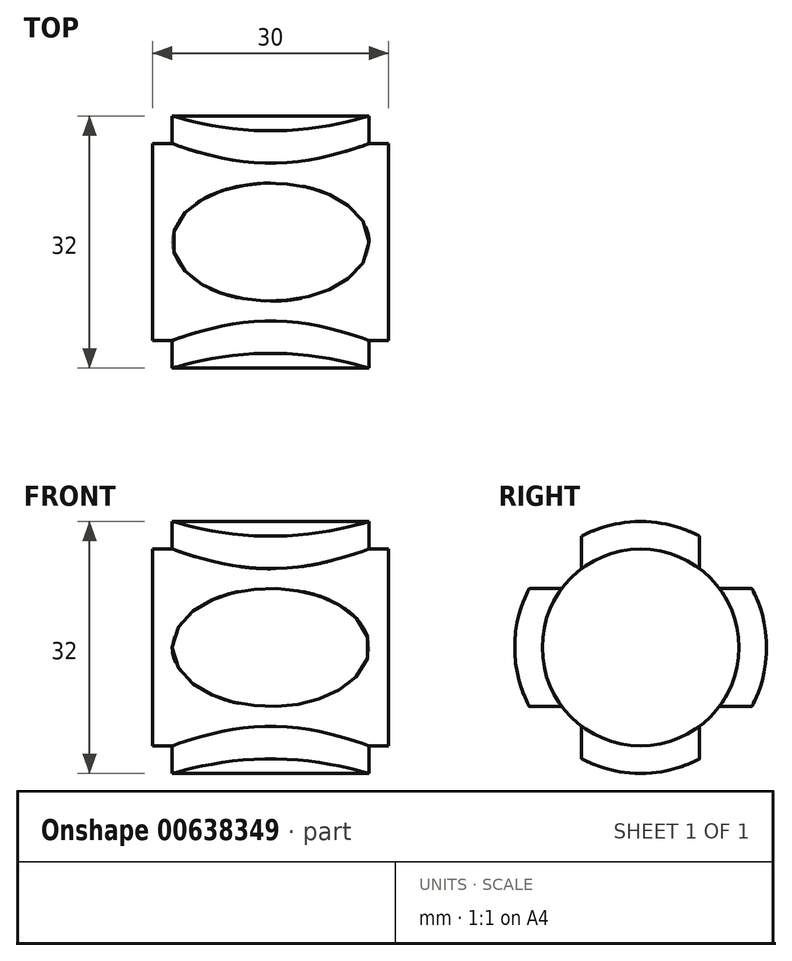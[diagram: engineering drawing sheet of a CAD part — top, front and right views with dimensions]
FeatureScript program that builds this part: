
annotation { "Feature Type Name" : "Feature", "Feature Type Description" : "" }
export const myFeature = defineFeature(function(context is Context, id is Id, definition is map)
    precondition{}
    {
        {
            var Q0;
            Q0=qCreatedBy(makeId("Right.planeOp"),FACE);
            var sketch = newSketch(context, id + "F0", { "sketchPlane" : qUnion([Q0])});
            skLineSegment(sketch, "E0.bottom", {"start": v(-5, 5) * mm, "end": v(5, 5) * mm});
            skLineSegment(sketch, "E0.top", {"start": v(-5, -5) * mm, "end": v(5, -5) * mm});
            skLineSegment(sketch, "E0.left", {"start": v(-5, 5) * mm, "end": v(-5, -5) * mm});
            skLineSegment(sketch, "E0.right", {"start": v(5, 5) * mm, "end": v(5, -5) * mm});
            skSolve(sketch);
        }
        {
            var Q0;
            Q0=makeQuery(id+"F0.imprint","IMPRINT",FACE,{"disambiguationData":[TD([[makeQuery(id+"F0.imprint","IMPRINT",EDGE,{"derivedFrom":sQuery(id+"F0.wireOp",EDGE,"E0.bottom")}),-1.0]])]});
            extrude(context, id + "F1", {"entities" : qUnion([Q0]), "endBound" : BoundingType.SYMMETRIC, "depth" : 30 * mm, "offsetDistance" : 25 * mm});
        }
        {
            var Q0;
            Q0=makeQuery(id+"F1.opExtrude","SWEPT_FACE",FACE,{"disambiguationData":[OSD([sQuery(id+"F0.wireOp",EDGE,"E0.bottom")])]});
            var sketch = newSketch(context, id + "F2", { "sketchPlane" : qUnion([Q0])});
            skText(sketch, "E1", { "text": "3D", "fontName": "OpenSans-Bold.ttf"});
            const initialGuessF2  = {"E1": [-0.00737, -0.00415, 1, 0, 0.00816]};
            skSetInitialGuess(sketch, initialGuessF2);
            skSolve(sketch);
        }
        {
            var Q0;
            Q0=makeQuery(id+"F1.opExtrude","SWEPT_FACE",FACE,{"disambiguationData":[OSD([sQuery(id+"F0.wireOp",EDGE,"E0.left")])]});
            var sketch = newSketch(context, id + "F3", { "sketchPlane" : qUnion([Q0])});
            skText(sketch, "E2", { "text": "3D", "fontName": "OpenSans-Bold.ttf"});
            const initialGuessF3  = {"E2": [-0.00747, -0.004, 1, 0, 0.00816]};
            skSetInitialGuess(sketch, initialGuessF3);
            skSolve(sketch);
        }
        {
            var Q0;
            Q0=makeQuery(id+"F1.opExtrude","SWEPT_FACE",FACE,{"disambiguationData":[OSD([sQuery(id+"F0.wireOp",EDGE,"E0.top")])]});
            var sketch = newSketch(context, id + "F4", { "sketchPlane" : qUnion([Q0])});
            skText(sketch, "E3", { "text": "3D", "fontName": "OpenSans-Bold.ttf"});
            const initialGuessF4  = {"E3": [-0.00747, -0.00412, 1, 0, 0.00816]};
            skSetInitialGuess(sketch, initialGuessF4);
            skSolve(sketch);
        }
        {
            var Q0;
            Q0=makeQuery(id+"F1.opExtrude","SWEPT_FACE",FACE,{"disambiguationData":[OSD([sQuery(id+"F0.wireOp",EDGE,"E0.right")])]});
            var sketch = newSketch(context, id + "F5", { "sketchPlane" : qUnion([Q0])});
            skText(sketch, "E4", { "text": "3D", "fontName": "OpenSans-Bold.ttf"});
            const initialGuessF5  = {"E4": [-0.0075, -0.0041, 1, 0, 0.00816]};
            skSetInitialGuess(sketch, initialGuessF5);
            skSolve(sketch);
        }
        {
            var Q0;
            Q0 = qSketchRegion(id + "F5", true);
            extrude(context, id + "F6", {"entities" : qUnion([Q0]), "operationType" : NewBodyOperationType.ADD, "depth" : 25 * mm, "offsetDistance" : 25 * mm});
        }
        {
            var Q0;
            Q0 = qSketchRegion(id + "F3", true);
            extrude(context, id + "F7", {"entities" : qUnion([Q0]), "operationType" : NewBodyOperationType.ADD, "depth" : 25 * mm, "offsetDistance" : 25 * mm});
        }
        {
            var Q0;
            Q0 = qSketchRegion(id + "F2", true);
            extrude(context, id + "F8", {"entities" : qUnion([Q0]), "operationType" : NewBodyOperationType.ADD, "depth" : 25 * mm, "offsetDistance" : 25 * mm});
        }
        {
            var Q0;
            Q0 = qSketchRegion(id + "F4", true);
            extrude(context, id + "F9", {"entities" : qUnion([Q0]), "operationType" : NewBodyOperationType.ADD, "depth" : 25 * mm, "offsetDistance" : 25 * mm});
        }
        {
            var Q0;
            Q0=qCreatedBy(makeId("Right.planeOp"),FACE);
            var sketch = newSketch(context, id + "F10", { "sketchPlane" : qUnion([Q0])});
            skCircle(sketch, "E5", {"center": v(0, 0) * mm, "radius": 12.5 * mm});
            skSolve(sketch);
        }
        {
            var Q0;
            Q0=makeQuery(id+"F10.imprint","IMPRINT",FACE,{"disambiguationData":[TD([[makeQuery(id+"F10.imprint","IMPRINT",EDGE,{"derivedFrom":sQuery(id+"F10.wireOp",EDGE,"E5")}),1.0]])]});
            extrude(context, id + "F11", {"entities" : qUnion([Q0]), "operationType" : NewBodyOperationType.ADD, "endBound" : BoundingType.SYMMETRIC, "depth" : 30 * mm, "offsetDistance" : 25 * mm});
        }
        {
            var Q0;
            Q0=qCreatedBy(makeId("Right.planeOp"),FACE);
            var sketch = newSketch(context, id + "F12", { "sketchPlane" : qUnion([Q0])});
            skCircle(sketch, "E6", {"center": v(0, 0) * mm, "radius": 14 * mm});
            skCircle(sketch, "E7", {"center": v(0, 0) * mm, "radius": 31.04 * mm});
            skSolve(sketch);
        }
        {
            var Q0;
            Q0=makeQuery(id+"F12.imprint","IMPRINT",FACE,{"disambiguationData":[TD([[makeQuery(id+"F12.imprint","IMPRINT",EDGE,{"derivedFrom":sQuery(id+"F12.wireOp",EDGE,"E6")}),-1.0]])]});
            extrude(context, id + "F13", {"entities" : qUnion([Q0]), "operationType" : NewBodyOperationType.REMOVE, "endBound" : BoundingType.SYMMETRIC, "oppositeDirection" : true, "depth" : 25 * mm, "offsetDistance" : 25 * mm});
        }
        {
            var Q0;
            Q0=qCreatedBy(makeId("Top.planeOp"),FACE);
            var sketch = newSketch(context, id + "F14", { "sketchPlane" : qUnion([Q0])});
            skEllipse(sketch, "E8", {"center": v(0, 0) * mm, "majorRadius": 12.5 * mm, "minorRadius": 7.5 * mm, "majorAxis": v(1, 0)});
            skFitSpline(sketch, "E9.0", {"points": [v(13.45, -0.9) * mm, v(13.52, 0) * mm, v(13.45, 0.9) * mm, v(13.16, 2.08) * mm, v(12.6, 3.19) * mm, v(11.8, 4.2) * mm, v(10.84, 5.16) * mm, v(9.4, 6.2) * mm, v(7.7, 7.04) * mm, v(6.2, 7.58) * mm, v(4.64, 8.02) * mm, v(2.99, 8.32) * mm, v(1.3, 8.47) * mm, v(0, 8.51) * mm, v(-1.3, 8.47) * mm, v(-2.99, 8.32) * mm, v(-4.64, 8.02) * mm, v(-6.2, 7.58) * mm, v(-7.7, 7.04) * mm, v(-9.4, 6.2) * mm, v(-10.84, 5.16) * mm, v(-11.8, 4.2) * mm, v(-12.6, 3.19) * mm, v(-13.16, 2.08) * mm, v(-13.45, 0.9) * mm, v(-13.52, 0) * mm, v(-13.45, -0.9) * mm, v(-13.16, -2.08) * mm, v(-12.6, -3.19) * mm, v(-11.8, -4.2) * mm, v(-10.84, -5.16) * mm, v(-9.4, -6.2) * mm, v(-7.7, -7.04) * mm, v(-6.2, -7.58) * mm, v(-4.64, -8.02) * mm, v(-2.99, -8.32) * mm, v(-1.3, -8.47) * mm, v(0, -8.51) * mm, v(1.3, -8.47) * mm, v(2.99, -8.32) * mm, v(4.64, -8.02) * mm, v(6.2, -7.58) * mm, v(7.7, -7.04) * mm, v(9.4, -6.2) * mm, v(10.84, -5.16) * mm, v(11.8, -4.2) * mm, v(12.6, -3.19) * mm, v(13.16, -2.08) * mm, v(13.45, -0.9) * mm, v(13.52, 0) * mm, v(13.45, 0.9) * mm, v(13.45, -0.9) * mm]});
            skSolve(sketch);
        }
        {
            var Q0;
            Q0 = qSketchRegion(id + "F14", true);
            extrude(context, id + "F15", {"entities" : qUnion([Q0]), "operationType" : NewBodyOperationType.ADD, "endBound" : BoundingType.SYMMETRIC, "depth" : 34.4 * mm, "offsetDistance" : 25 * mm});
        }
        {
            var Q0;
            Q0=qCreatedBy(makeId("Front.planeOp"),FACE);
            var sketch = newSketch(context, id + "F16", { "sketchPlane" : qUnion([Q0])});
            skEllipse(sketch, "E10", {"center": v(0, 0) * mm, "majorRadius": 12.5 * mm, "minorRadius": 7.5 * mm, "majorAxis": v(-1, 0)});
            skFitSpline(sketch, "E11.0", {"points": [v(-13.45, 0.9) * mm, v(-13.52, 0) * mm, v(-13.45, -0.9) * mm, v(-13.16, -2.08) * mm, v(-12.6, -3.19) * mm, v(-11.8, -4.2) * mm, v(-10.84, -5.16) * mm, v(-9.4, -6.2) * mm, v(-7.7, -7.04) * mm, v(-6.2, -7.58) * mm, v(-4.64, -8.02) * mm, v(-2.99, -8.32) * mm, v(-1.3, -8.47) * mm, v(0, -8.51) * mm, v(1.3, -8.47) * mm, v(2.99, -8.32) * mm, v(4.64, -8.02) * mm, v(6.2, -7.58) * mm, v(7.7, -7.04) * mm, v(9.4, -6.2) * mm, v(10.84, -5.16) * mm, v(11.8, -4.2) * mm, v(12.6, -3.19) * mm, v(13.16, -2.08) * mm, v(13.45, -0.9) * mm, v(13.52, 0) * mm, v(13.45, 0.9) * mm, v(13.16, 2.08) * mm, v(12.6, 3.19) * mm, v(11.8, 4.2) * mm, v(10.84, 5.16) * mm, v(9.4, 6.2) * mm, v(7.7, 7.04) * mm, v(6.2, 7.58) * mm, v(4.64, 8.02) * mm, v(2.99, 8.32) * mm, v(1.3, 8.47) * mm, v(0, 8.51) * mm, v(-1.3, 8.47) * mm, v(-2.99, 8.32) * mm, v(-4.64, 8.02) * mm, v(-6.2, 7.58) * mm, v(-7.7, 7.04) * mm, v(-9.4, 6.2) * mm, v(-10.84, 5.16) * mm, v(-11.8, 4.2) * mm, v(-12.6, 3.19) * mm, v(-13.16, 2.08) * mm, v(-13.45, 0.9) * mm, v(-13.52, 0) * mm, v(-13.45, -0.9) * mm, v(-13.45, 0.9) * mm]});
            skSolve(sketch);
        }
        {
            var Q0;
            Q0 = qSketchRegion(id + "F16", true);
            extrude(context, id + "F17", {"entities" : qUnion([Q0]), "operationType" : NewBodyOperationType.ADD, "endBound" : BoundingType.SYMMETRIC, "depth" : 34 * mm, "offsetDistance" : 25 * mm});
        }
        {
            var Q0;
            Q0=qCreatedBy(makeId("Right.planeOp"),FACE);
            var sketch = newSketch(context, id + "F18", { "sketchPlane" : qUnion([Q0])});
            skCircle(sketch, "E12", {"center": v(0, 0) * mm, "radius": 16 * mm});
            skCircle(sketch, "E13", {"center": v(0, 0) * mm, "radius": 21.54 * mm});
            skSolve(sketch);
        }
        {
            var Q0;
            Q0 = qSketchRegion(id + "F18", true);
            extrude(context, id + "F19", {"entities" : qUnion([Q0]), "operationType" : NewBodyOperationType.REMOVE, "endBound" : BoundingType.SYMMETRIC, "depth" : 30.6 * mm, "offsetDistance" : 25 * mm});
        }
    });
